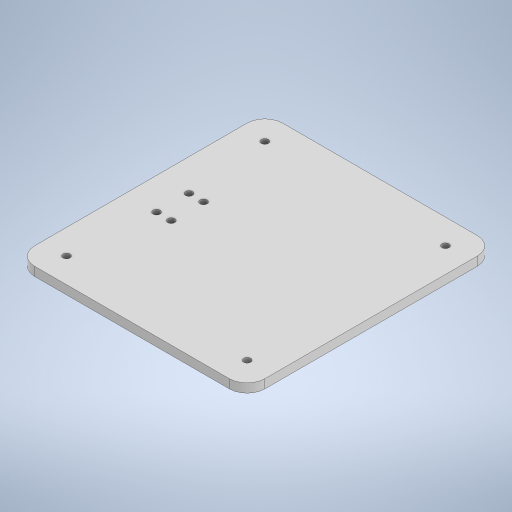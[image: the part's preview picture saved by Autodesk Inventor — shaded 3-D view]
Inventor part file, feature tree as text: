
AUTODESK INVENTOR PART (.ipt)
format: ipt  version: 2023.1 (Build 271208000, 208)  size: 236,544 bytes
history: native  units: mm
features: extrude x1, fillet x1, sketch x1
ambient origin geometry x8: Origin, YZ Plane, XZ Plane, XY Plane, X Axis, Y Axis, Z Axis, Center Point
bodies: Solid1 (feature_tree)
feature tree (3):
  extrude  "Extrusion1"  Depth=130.0mm
  fillet  "Fillet1"  Radius=4.0mm
  sketch  "Sketch1"  dims[d0=140.0mm d1=130.0mm d2=4.0mm d3=14.0mm d4=14.0mm d5=70.0mm d6=65.0mm d9=18.0mm d10=4.0mm d11=9.15mm d12=4.0mm d13=9.15mm d14=8.25mm d15=5.0mm d16=0.0mm d17=10.0mm]
